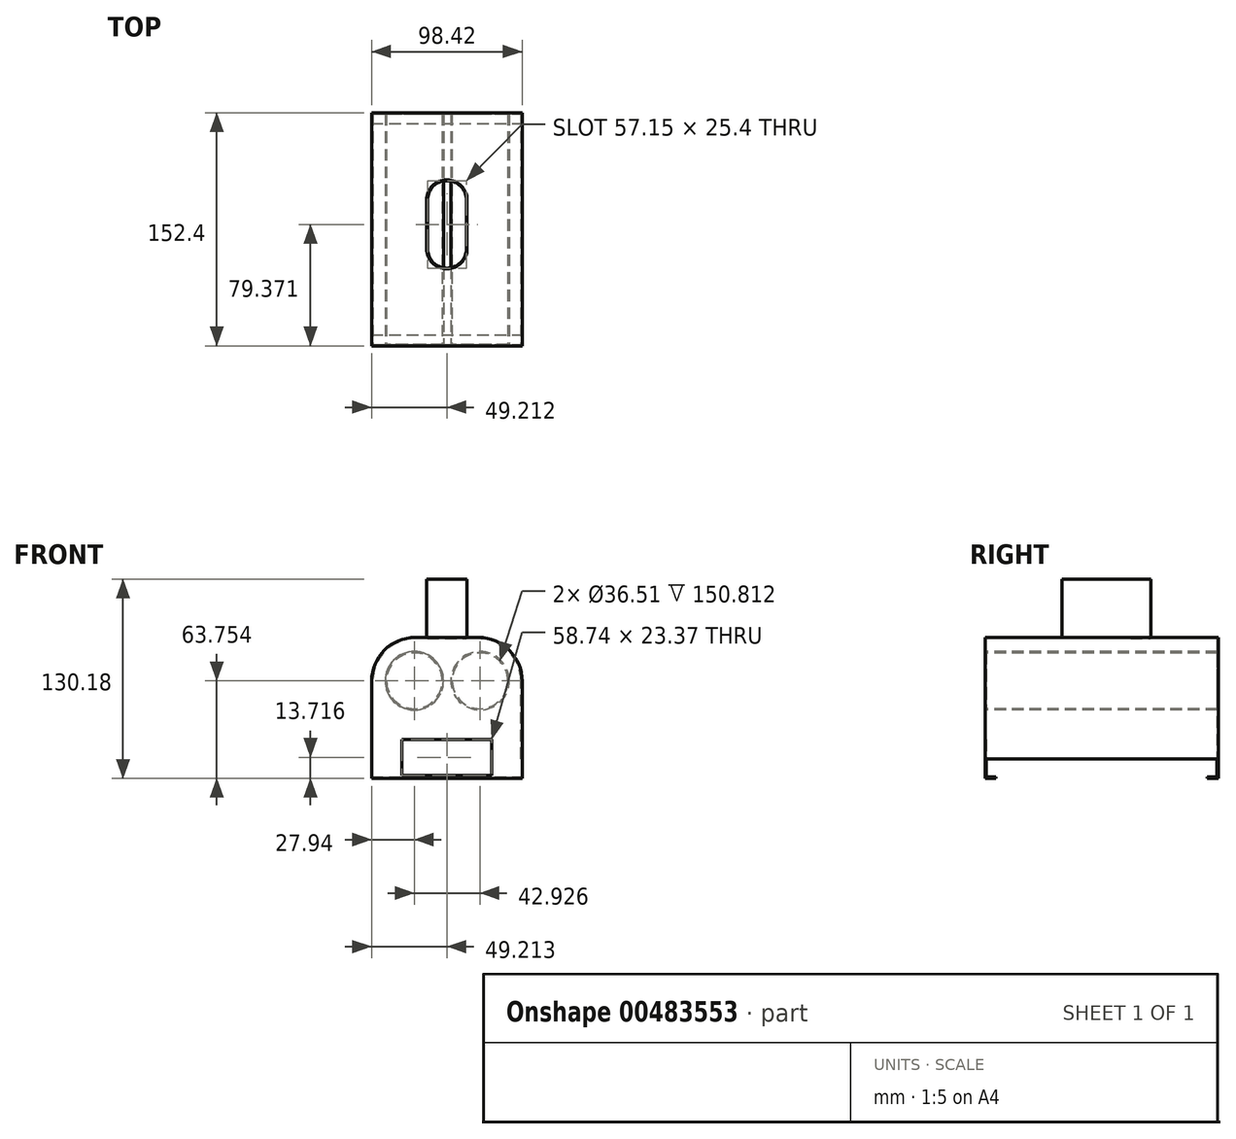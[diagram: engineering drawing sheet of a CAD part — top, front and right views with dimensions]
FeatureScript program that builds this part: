
annotation { "Feature Type Name" : "Feature", "Feature Type Description" : "" }
export const myFeature = defineFeature(function(context is Context, id is Id, definition is map)
    precondition{}
    {
        {
            var Q0;
            Q0=qCreatedBy(makeId("Front.planeOp"),FACE);
            var sketch = newSketch(context, id + "F0", { "sketchPlane" : qUnion([Q0])});
            skLineSegment(sketch, "E0.bottom", {"start": v(0, 0) * mm, "end": v(98.43, 0) * mm});
            skLineSegment(sketch, "E0.top", {"start": v(0, 92.08) * mm, "end": v(98.42, 92.08) * mm});
            skLineSegment(sketch, "E0.left", {"start": v(0, 0) * mm, "end": v(0, 92.08) * mm});
            skLineSegment(sketch, "E0.right", {"start": v(98.43, 0) * mm, "end": v(98.42, 92.08) * mm});
            skLineSegment(sketch, "E1.bottom", {"start": v(19.84, 25.4) * mm, "end": v(78.58, 25.4) * mm});
            skLineSegment(sketch, "E1.top", {"start": v(19.84, 2.03) * mm, "end": v(78.58, 2.03) * mm});
            skLineSegment(sketch, "E1.left", {"start": v(19.84, 25.4) * mm, "end": v(19.84, 2.03) * mm});
            skLineSegment(sketch, "E1.right", {"start": v(78.58, 25.4) * mm, "end": v(78.58, 2.03) * mm});
            skSolve(sketch);
        }
        {
            var Q0;
            Q0 = qSketchRegion(id + "F0", true);
            extrude(context, id + "F1", {"entities" : qUnion([Q0]), "depth" : 0.8 * mm});
        }
        {
            var Q0;
            Q0=makeQuery(id+"F1.opExtrude","SWEPT_EDGE",EDGE,{"disambiguationData":[OSD([sQuery(id+"F0.wireOp",EDGE,"E0.top"),sQuery(id+"F0.wireOp",EDGE,"E0.left")])]});
            var Q1;
            Q1=makeQuery(id+"F1.opExtrude","SWEPT_EDGE",EDGE,{"disambiguationData":[OSD([sQuery(id+"F0.wireOp",EDGE,"E0.top"),sQuery(id+"F0.wireOp",EDGE,"E0.right")])]});
            fillet(context, id + "F2", {"entities" : qUnion([Q0, Q1]), "radius" : 28.57 * mm, "tangentPropagation" : true, "allowEdgeOverflow" : false});
        }
        {
            var Q0;
            Q0=makeQuery(id+"F1.opExtrude","CAP_FACE",FACE,{"disambiguationData":[OSD([sQuery(id+"F0.wireOp",EDGE,"E0.bottom"),sQuery(id+"F0.wireOp",EDGE,"E0.top"),sQuery(id+"F0.wireOp",EDGE,"E0.left"),sQuery(id+"F0.wireOp",EDGE,"E0.right"),sQuery(id+"F0.wireOp",EDGE,"E1.bottom"),sQuery(id+"F0.wireOp",EDGE,"E1.top"),sQuery(id+"F0.wireOp",EDGE,"E1.left"),sQuery(id+"F0.wireOp",EDGE,"E1.right")])],"isStart":true});
            var sketch = newSketch(context, id + "F3", { "sketchPlane" : qUnion([Q0])});
            skCircle(sketch, "E2", {"center": v(-70.87, 63.75) * mm, "radius": 19.05 * mm});
            skCircle(sketch, "E3", {"center": v(-70.87, 63.75) * mm, "radius": 18.26 * mm});
            skCircle(sketch, "E4", {"center": v(-27.94, 63.75) * mm, "radius": 18.26 * mm});
            skCircle(sketch, "E5", {"center": v(-27.94, 63.75) * mm, "radius": 19.05 * mm});
            skLineSegment(sketch, "E6", {"start": v(-70.87, 63.75) * mm, "end": v(-27.94, 63.75) * mm, "construction": true});
            skSolve(sketch);
        }
        {
            var Q0;
            Q0 = qSketchRegion(id + "F3", true);
            extrude(context, id + "F4", {"entities" : qUnion([Q0]), "operationType" : NewBodyOperationType.ADD, "depth" : 150.8 * mm});
        }
        {
            var Q0;
            Q0=makeQuery(id+"F4.opExtrude","CAP_FACE",FACE,{"disambiguationData":[OSD([sQuery(id+"F3.wireOp",EDGE,"E4"),sQuery(id+"F3.wireOp",EDGE,"E5")])],"isStart":false});
            var sketch = newSketch(context, id + "F5", { "sketchPlane" : qUnion([Q0])});
            skLineSegment(sketch, "E7.bottom", {"start": v(0, 0) * mm, "end": v(-98.43, 0) * mm});
            skLineSegment(sketch, "E7.top", {"start": v(0, 92.08) * mm, "end": v(-98.43, 92.08) * mm});
            skLineSegment(sketch, "E7.left", {"start": v(0, 0) * mm, "end": v(0, 92.08) * mm});
            skLineSegment(sketch, "E7.right", {"start": v(-98.43, 0) * mm, "end": v(-98.43, 92.08) * mm});
            skSolve(sketch);
        }
        {
            var Q0;
            Q0 = qSketchRegion(id + "F5", true);
            extrude(context, id + "F6", {"entities" : qUnion([Q0]), "operationType" : NewBodyOperationType.ADD, "depth" : 0.8 * mm});
        }
        {
            var Q0;
            Q0=makeQuery(id+"F6.opExtrude","SWEPT_EDGE",EDGE,{"disambiguationData":[OSD([sQuery(id+"F5.wireOp",EDGE,"E7.top"),sQuery(id+"F5.wireOp",EDGE,"E7.left")])]});
            var Q1;
            Q1=makeQuery(id+"F6.opExtrude","SWEPT_EDGE",EDGE,{"disambiguationData":[OSD([sQuery(id+"F5.wireOp",EDGE,"E7.top"),sQuery(id+"F5.wireOp",EDGE,"E7.right")])]});
            fillet(context, id + "F7", {"entities" : qUnion([Q0, Q1]), "radius" : 28.57 * mm, "tangentPropagation" : true, "allowEdgeOverflow" : false});
        }
        {
            var Q0;
            {var subQ0=sQuery(id+"F0.wireOp",EDGE,"E1.right");var subQ1=sQuery(id+"F0.wireOp",EDGE,"E0.left");var subQ2=sQuery(id+"F0.wireOp",EDGE,"E0.top");var subQ3=sQuery(id+"F0.wireOp",EDGE,"E1.left");var subQ4=sQuery(id+"F0.wireOp",EDGE,"E1.top");var subQ5=sQuery(id+"F0.wireOp",EDGE,"E1.bottom");var subQ6=sQuery(id+"F0.wireOp",EDGE,"E0.bottom");var subQ7=sQuery(id+"F0.wireOp",EDGE,"E0.right");Q0=makeQuery(id+"F4.boolean.opBoolean","SPLIT",FACE,{"disambiguationData":[TD([makeQuery(id+"F1.opExtrude","SWEPT_FACE",FACE,{"disambiguationData":[OSD([subQ6])]})])],"derivedFrom":makeQuery(id+"F1.opExtrude","CAP_FACE",FACE,{"disambiguationData":[OSD([subQ6,subQ2,subQ1,subQ7,subQ5,subQ4,subQ3,subQ0])],"isStart":true})});}
            var sketch = newSketch(context, id + "F8", { "sketchPlane" : qUnion([Q0])});
            skLineSegment(sketch, "E8.bottom", {"start": v(0, 0) * mm, "end": v(-98.43, 0) * mm});
            skLineSegment(sketch, "E8.top", {"start": v(0, 0.8) * mm, "end": v(-98.43, 0.8) * mm});
            skLineSegment(sketch, "E8.left", {"start": v(0, 0) * mm, "end": v(0, 0.8) * mm});
            skLineSegment(sketch, "E8.right", {"start": v(-98.43, 0) * mm, "end": v(-98.43, 0.8) * mm});
            skSolve(sketch);
        }
        {
            var Q0;
            Q0 = qSketchRegion(id + "F8", true);
            extrude(context, id + "F9", {"entities" : qUnion([Q0]), "operationType" : NewBodyOperationType.ADD, "depth" : 6.35 * mm});
        }
        {
            var Q0;
            {var subQ0=sQuery(id+"F5.wireOp",EDGE,"E7.bottom");var subQ1=sQuery(id+"F5.wireOp",EDGE,"E7.top");var subQ2=sQuery(id+"F5.wireOp",EDGE,"E7.left");var subQ3=sQuery(id+"F5.wireOp",EDGE,"E7.right");Q0=makeQuery(id+"F6.boolean.opBoolean","SPLIT",FACE,{"disambiguationData":[TD([makeQuery(id+"F4.opExtrude","SWEPT_FACE",FACE,{"disambiguationData":[OSD([sQuery(id+"F3.wireOp",EDGE,"E2")])]})])],"derivedFrom":makeQuery(id+"F6.opExtrude","CAP_FACE",FACE,{"disambiguationData":[OSD([subQ0,subQ1,subQ2,subQ3])],"isStart":true})});}
            var sketch = newSketch(context, id + "F10", { "sketchPlane" : qUnion([Q0])});
            skLineSegment(sketch, "E9.bottom", {"start": v(0, 0) * mm, "end": v(98.43, 0) * mm});
            skLineSegment(sketch, "E9.top", {"start": v(0, 0.8) * mm, "end": v(98.43, 0.8) * mm});
            skLineSegment(sketch, "E9.left", {"start": v(0, 0) * mm, "end": v(0, 0.8) * mm});
            skLineSegment(sketch, "E9.right", {"start": v(98.43, 0) * mm, "end": v(98.43, 0.8) * mm});
            skSolve(sketch);
        }
        {
            var Q0;
            Q0 = qSketchRegion(id + "F10", true);
            extrude(context, id + "F11", {"entities" : qUnion([Q0]), "operationType" : NewBodyOperationType.ADD, "depth" : 6.35 * mm});
        }
        {
            var Q0;
            {var subQ0=sQuery(id+"F0.wireOp",EDGE,"E1.right");var subQ1=sQuery(id+"F0.wireOp",EDGE,"E0.left");var subQ2=sQuery(id+"F0.wireOp",EDGE,"E0.top");var subQ3=sQuery(id+"F0.wireOp",EDGE,"E1.left");var subQ4=sQuery(id+"F0.wireOp",EDGE,"E1.top");var subQ5=sQuery(id+"F0.wireOp",EDGE,"E1.bottom");var subQ6=sQuery(id+"F0.wireOp",EDGE,"E0.bottom");var subQ7=sQuery(id+"F0.wireOp",EDGE,"E0.right");Q0=makeQuery(id+"F4.boolean.opBoolean","SPLIT",FACE,{"disambiguationData":[TD([makeQuery(id+"F1.opExtrude","SWEPT_FACE",FACE,{"disambiguationData":[OSD([subQ6])]})])],"derivedFrom":makeQuery(id+"F1.opExtrude","CAP_FACE",FACE,{"disambiguationData":[OSD([subQ6,subQ2,subQ1,subQ7,subQ5,subQ4,subQ3,subQ0])],"isStart":true})});}
            var sketch = newSketch(context, id + "F12", { "sketchPlane" : qUnion([Q0])});
            skLineSegment(sketch, "E10", {"start": v(-98.43, 12.7) * mm, "end": v(-98.43, 63.5) * mm});
            skLineSegment(sketch, "E11", {"start": v(-69.85, 92.08) * mm, "end": v(-28.58, 92.08) * mm});
            skLineSegment(sketch, "E12", {"start": v(0, 12.7) * mm, "end": v(0, 63.5) * mm});
            skArc(sketch, "E13", {"start": v(-69.85, 91.28) * mm, "mid": v(-89.5, 83.14) * mm, "end": v(-97.63, 63.5) * mm});
            skLineSegment(sketch, "E14", {"start": v(-98.43, 12.7) * mm, "end": v(-97.63, 12.7) * mm});
            skLineSegment(sketch, "E15", {"start": v(-97.63, 12.7) * mm, "end": v(-97.63, 63.5) * mm});
            skLineSegment(sketch, "E16", {"start": v(0, 12.7) * mm, "end": v(-0.8, 12.7) * mm});
            skLineSegment(sketch, "E17", {"start": v(-0.8, 12.7) * mm, "end": v(-0.8, 63.5) * mm});
            skArc(sketch, "E18.trimOffspring", {"start": v(0, 63.5) * mm, "mid": v(-8.37, 83.7) * mm, "end": v(-28.58, 92.08) * mm});
            skArc(sketch, "E19.trimOffspring", {"start": v(-0.8, 63.5) * mm, "mid": v(-8.93, 83.14) * mm, "end": v(-28.58, 91.28) * mm});
            skLineSegment(sketch, "E20", {"start": v(-28.58, 91.28) * mm, "end": v(-69.85, 91.28) * mm});
            skArc(sketch, "E21.trimOffspring", {"start": v(-69.85, 92.08) * mm, "mid": v(-92.3, 81.18) * mm, "end": v(-97.63, 56.81) * mm});
            skSolve(sketch);
        }
        {
            var Q0;
            Q0 = qSketchRegion(id + "F12", true);
            extrude(context, id + "F13", {"entities" : qUnion([Q0]), "operationType" : NewBodyOperationType.ADD, "depth" : 151.57 * mm});
        }
        {
            var Q0;
            Q0=makeQuery(id+"F13.boolean.opBoolean","MERGE",FACE,{"derivedFrom":[makeQuery(id+"F1.opExtrude","SWEPT_FACE",FACE,{"disambiguationData":[OSD([sQuery(id+"F0.wireOp",EDGE,"E0.top")])]}),makeQuery(id+"F6.opExtrude","SWEPT_FACE",FACE,{"disambiguationData":[OSD([sQuery(id+"F5.wireOp",EDGE,"E7.top")])]}),makeQuery(id+"F13.opExtrude","SWEPT_FACE",FACE,{"disambiguationData":[OSD([sQuery(id+"F12.wireOp",EDGE,"E11")])]})]});
            var sketch = newSketch(context, id + "F14", { "sketchPlane" : qUnion([Q0])});
            skLineSegment(sketch, "E22", {"start": v(49.21, 62.7) * mm, "end": v(49.21, 94.46) * mm, "construction": true});
            skArc(sketch, "E23", {"start": v(61.91, 94.46) * mm, "mid": v(49.21, 107.16) * mm, "end": v(36.51, 94.46) * mm});
            skArc(sketch, "E24", {"start": v(36.51, 62.7) * mm, "mid": v(49.21, 50) * mm, "end": v(61.91, 62.7) * mm});
            skLineSegment(sketch, "E25", {"start": v(36.51, 62.7) * mm, "end": v(36.51, 94.46) * mm});
            skLineSegment(sketch, "E26", {"start": v(61.91, 62.7) * mm, "end": v(61.91, 94.46) * mm});
            skSolve(sketch);
        }
        {
            var Q0;
            Q0 = qSketchRegion(id + "F14", true);
            extrude(context, id + "F15", {"entities" : qUnion([Q0]), "operationType" : NewBodyOperationType.REMOVE, "oppositeDirection" : true, "depth" : 2.54 * mm, "offsetDistance" : 25.4 * mm});
        }
        {
            var Q0;
            Q0=makeQuery(id+"F13.boolean.opBoolean","MERGE",FACE,{"derivedFrom":[makeQuery(id+"F1.opExtrude","SWEPT_FACE",FACE,{"disambiguationData":[OSD([sQuery(id+"F0.wireOp",EDGE,"E0.top")])]}),makeQuery(id+"F6.opExtrude","SWEPT_FACE",FACE,{"disambiguationData":[OSD([sQuery(id+"F5.wireOp",EDGE,"E7.top")])]}),makeQuery(id+"F13.opExtrude","SWEPT_FACE",FACE,{"disambiguationData":[OSD([sQuery(id+"F12.wireOp",EDGE,"E11")])]})]});
            var sketch = newSketch(context, id + "F16", { "sketchPlane" : qUnion([Q0])});
            skLineSegment(sketch, "E27", {"start": v(49.21, 62.7) * mm, "end": v(49.21, 94.46) * mm, "construction": true});
            skArc(sketch, "E28", {"start": v(61.91, 94.46) * mm, "mid": v(49.21, 107.16) * mm, "end": v(36.51, 94.46) * mm});
            skArc(sketch, "E29", {"start": v(36.51, 62.7) * mm, "mid": v(49.21, 50) * mm, "end": v(61.91, 62.7) * mm});
            skLineSegment(sketch, "E30", {"start": v(36.51, 62.7) * mm, "end": v(36.51, 94.46) * mm});
            skLineSegment(sketch, "E31", {"start": v(61.91, 62.7) * mm, "end": v(61.91, 94.46) * mm});
            skArc(sketch, "E32", {"start": v(35.95, 62.7) * mm, "mid": v(49.21, 49.45) * mm, "end": v(62.47, 62.7) * mm});
            skArc(sketch, "E33", {"start": v(62.47, 94.46) * mm, "mid": v(49.21, 107.72) * mm, "end": v(35.95, 94.46) * mm});
            skLineSegment(sketch, "E34", {"start": v(35.95, 62.7) * mm, "end": v(35.95, 94.46) * mm});
            skLineSegment(sketch, "E35", {"start": v(62.47, 62.7) * mm, "end": v(62.47, 94.46) * mm});
            skSolve(sketch);
        }
        {
            var Q0;
            Q0 = qSketchRegion(id + "F16", true);
            extrude(context, id + "F17", {"entities" : qUnion([Q0]), "operationType" : NewBodyOperationType.ADD, "depth" : 38.1 * mm, "offsetDistance" : 25.4 * mm});
        }
    });
